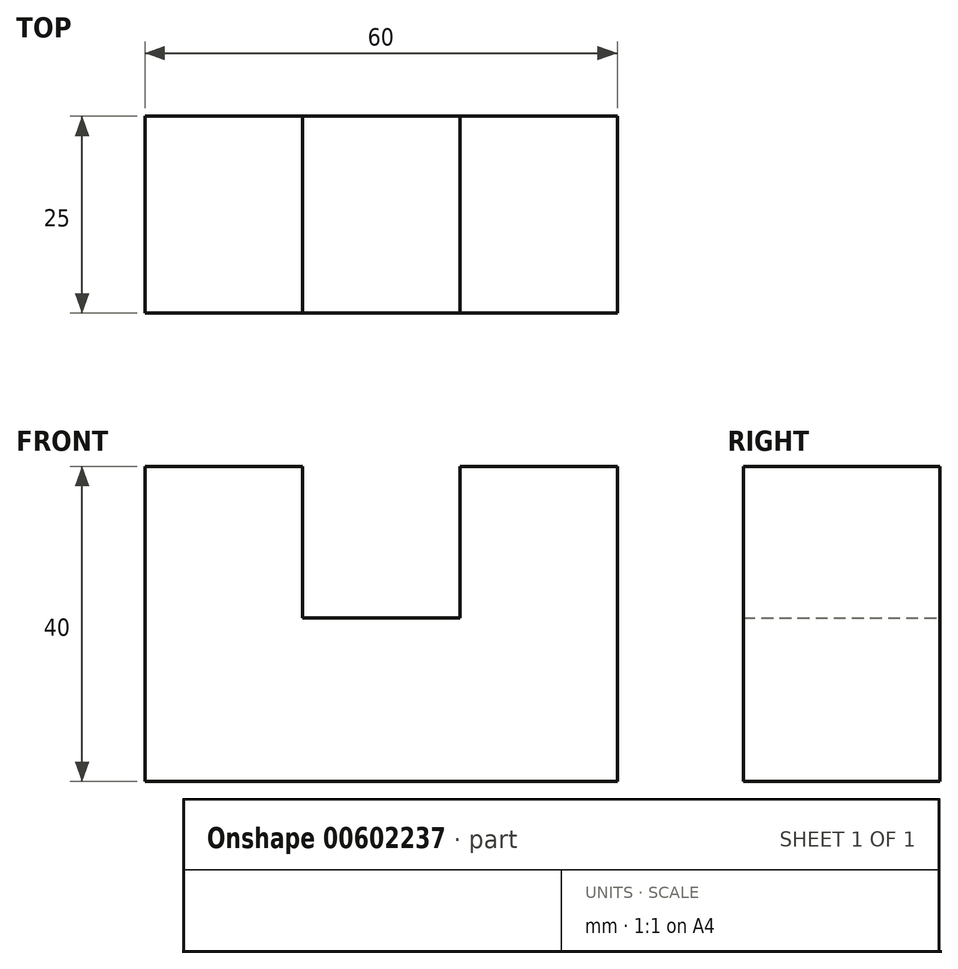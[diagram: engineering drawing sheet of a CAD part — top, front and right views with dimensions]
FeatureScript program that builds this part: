
annotation { "Feature Type Name" : "Feature", "Feature Type Description" : "" }
export const myFeature = defineFeature(function(context is Context, id is Id, definition is map)
    precondition{}
    {
        {
            var Q0;
            Q0=qCreatedBy(makeId("Front.planeOp"),FACE);
            var sketch = newSketch(context, id + "F0", { "sketchPlane" : qUnion([Q0])});
            skLineSegment(sketch, "E0", {"start": v(-40, -40) * mm, "end": v(20, -40) * mm});
            skLineSegment(sketch, "E1", {"start": v(20, -40) * mm, "end": v(20, 0) * mm});
            skLineSegment(sketch, "E2", {"start": v(20, 0) * mm, "end": v(0, 0) * mm});
            skLineSegment(sketch, "E3", {"start": v(0, 0) * mm, "end": v(0, -19.27) * mm});
            skLineSegment(sketch, "E4", {"start": v(0, -19.27) * mm, "end": v(-20, -19.27) * mm});
            skLineSegment(sketch, "E5", {"start": v(-20, -19.27) * mm, "end": v(-20, 0) * mm});
            skLineSegment(sketch, "E6", {"start": v(-20, 0) * mm, "end": v(-40, 0) * mm});
            skLineSegment(sketch, "E7", {"start": v(-40, 0) * mm, "end": v(-40, -40) * mm});
            skSolve(sketch);
        }
        {
            var Q0;
            Q0 = qSketchRegion(id + "F0", true);
            extrude(context, id + "F1", {"entities" : qUnion([Q0]), "depth" : 25 * mm, "offsetDistance" : 25 * mm});
        }
    });
